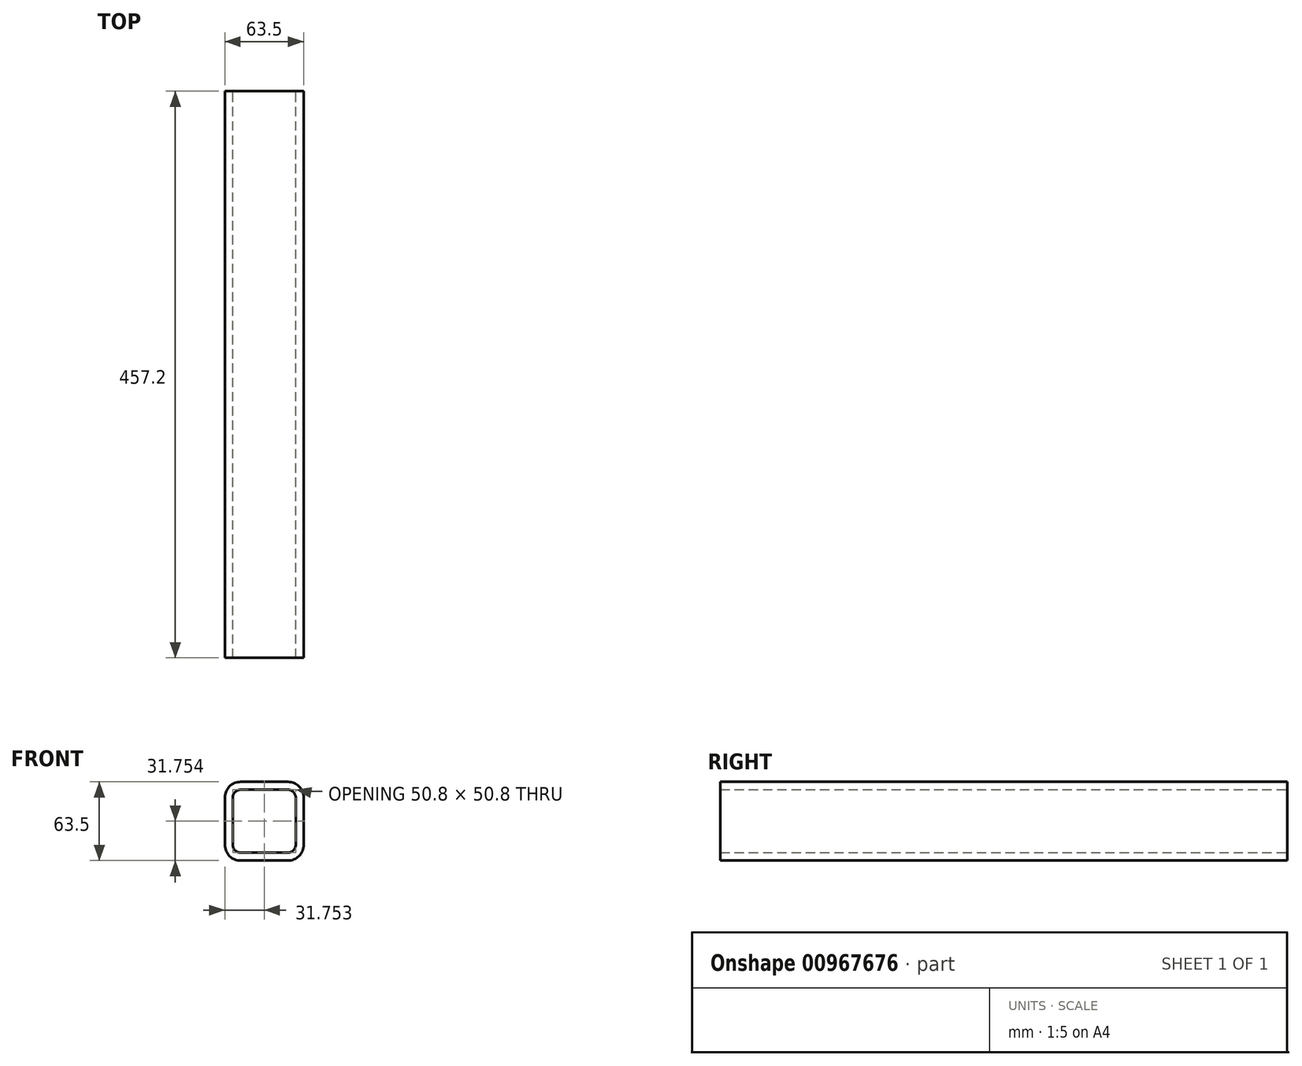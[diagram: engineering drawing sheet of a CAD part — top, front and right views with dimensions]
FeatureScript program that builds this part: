
annotation { "Feature Type Name" : "Feature", "Feature Type Description" : "" }
export const myFeature = defineFeature(function(context is Context, id is Id, definition is map)
    precondition{}
    {
        {
            var Q0;
            Q0=qCreatedBy(makeId("Front.planeOp"),FACE);
            var sketch = newSketch(context, id + "F0", { "sketchPlane" : qUnion([Q0])});
            skLineSegment(sketch, "E0.bottom", {"start": v(-144.7, 58.02) * mm, "end": v(-106.6, 58.02) * mm});
            skLineSegment(sketch, "E0.top", {"start": v(-144.7, 108.82) * mm, "end": v(-106.6, 108.82) * mm});
            skLineSegment(sketch, "E0.left", {"start": v(-151.05, 64.37) * mm, "end": v(-151.05, 102.47) * mm});
            skLineSegment(sketch, "E0.right", {"start": v(-100.25, 64.37) * mm, "end": v(-100.25, 102.47) * mm});
            skPoint(sketch, "E1.visualSharp", {"position": v(-151.05, 108.82) * mm});
            skArc(sketch, "E1.filletArc", {"start": v(-144.7, 108.82) * mm, "mid": v(-149.19, 106.96) * mm, "end": v(-151.05, 102.47) * mm});
            skPoint(sketch, "E2.visualSharp", {"position": v(-100.25, 108.82) * mm});
            skArc(sketch, "E2.filletArc", {"start": v(-100.25, 102.47) * mm, "mid": v(-102.1, 106.96) * mm, "end": v(-106.6, 108.82) * mm});
            skPoint(sketch, "E3.visualSharp", {"position": v(-100.25, 58.02) * mm});
            skArc(sketch, "E3.filletArc", {"start": v(-106.6, 58.02) * mm, "mid": v(-102.1, 59.88) * mm, "end": v(-100.25, 64.37) * mm});
            skPoint(sketch, "E4.visualSharp", {"position": v(-151.05, 58.02) * mm});
            skArc(sketch, "E4.filletArc", {"start": v(-151.05, 64.37) * mm, "mid": v(-149.19, 59.88) * mm, "end": v(-144.7, 58.02) * mm});
            skArc(sketch, "E5.0", {"start": v(-157.4, 64.37) * mm, "mid": v(-153.68, 55.4) * mm, "end": v(-144.7, 51.67) * mm});
            skLineSegment(sketch, "E5.1", {"start": v(-157.4, 64.37) * mm, "end": v(-157.4, 102.47) * mm});
            skLineSegment(sketch, "E5.2", {"start": v(-144.7, 51.67) * mm, "end": v(-106.6, 51.67) * mm});
            skArc(sketch, "E5.3", {"start": v(-144.7, 115.17) * mm, "mid": v(-153.68, 111.45) * mm, "end": v(-157.4, 102.47) * mm});
            skArc(sketch, "E5.4", {"start": v(-106.6, 51.67) * mm, "mid": v(-97.62, 55.4) * mm, "end": v(-93.9, 64.37) * mm});
            skLineSegment(sketch, "E5.5", {"start": v(-93.9, 64.37) * mm, "end": v(-93.9, 102.47) * mm});
            skArc(sketch, "E5.6", {"start": v(-93.9, 102.47) * mm, "mid": v(-97.62, 111.45) * mm, "end": v(-106.6, 115.17) * mm});
            skLineSegment(sketch, "E5.7", {"start": v(-144.7, 115.17) * mm, "end": v(-106.6, 115.17) * mm});
            skSolve(sketch);
        }
        {
            var Q0;
            Q0 = qSketchRegion(id + "F0", true);
            extrude(context, id + "F1", {"entities" : qUnion([Q0]), "depth" : 457.2 * mm, "offsetDistance" : 25.4 * mm});
        }
    });
